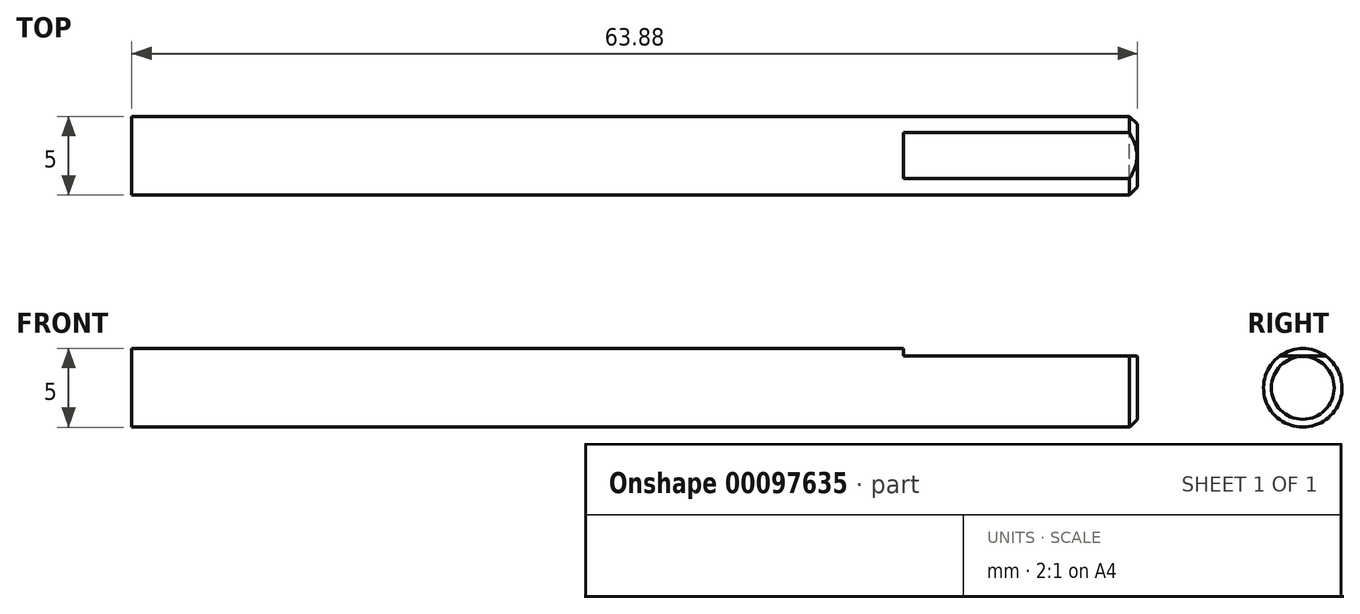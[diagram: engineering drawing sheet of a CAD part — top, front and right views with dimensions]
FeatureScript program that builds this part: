
annotation { "Feature Type Name" : "Feature", "Feature Type Description" : "" }
export const myFeature = defineFeature(function(context is Context, id is Id, definition is map)
    precondition{}
    {
        {
            var Q0;
            Q0=qCreatedBy(makeId("Right.planeOp"),FACE);
            var sketch = newSketch(context, id + "F0", { "sketchPlane" : qUnion([Q0])});
            skCircle(sketch, "E0", {"center": v(0, 0) * mm, "radius": 2.5 * mm});
            skLineSegment(sketch, "E1", {"start": v(-1.46, 2.02) * mm, "end": v(1.46, 2.02) * mm});
            skSolve(sketch);
        }
        {
            var Q0;
            {var subQ0=sQuery(id+"F0.wireOp",EDGE,"E1");Q0=makeQuery(id+"F0.imprint","IMPRINT",FACE,{"disambiguationData":[TD([[makeQuery(id+"F0.imprint","IMPRINT",EDGE,{"derivedFrom":subQ0}),-1.0]])]});}
            var Q1;
            {var subQ0=sQuery(id+"F0.wireOp",EDGE,"E1");Q1=makeQuery(id+"F0.imprint","IMPRINT",FACE,{"disambiguationData":[TD([[makeQuery(id+"F0.imprint","IMPRINT",EDGE,{"derivedFrom":subQ0}),1.0]])]});}
            extrude(context, id + "F1", {"entities" : qUnion([Q0, Q1]), "oppositeDirection" : true, "depth" : 49.02 * mm});
        }
        {
            var Q0;
            {var subQ0=sQuery(id+"F0.wireOp",EDGE,"E1");Q0=makeQuery(id+"F0.imprint","IMPRINT",FACE,{"disambiguationData":[TD([[makeQuery(id+"F0.imprint","IMPRINT",EDGE,{"derivedFrom":subQ0}),-1.0]])]});}
            extrude(context, id + "F2", {"entities" : qUnion([Q0]), "operationType" : NewBodyOperationType.ADD, "depth" : 14.86 * mm});
        }
        {
            var Q0;
            Q0=makeQuery(id+"F2.opExtrude","CAP_EDGE",EDGE,{"disambiguationData":[OSD([sQuery(id+"F0.wireOp",EDGE,"E0")])],"isStart":false});
            chamfer(context, id + "F3", {"entities" : qUnion([Q0]), "width" : 0.5 * mm, "tangentPropagation" : true});
        }
    });
